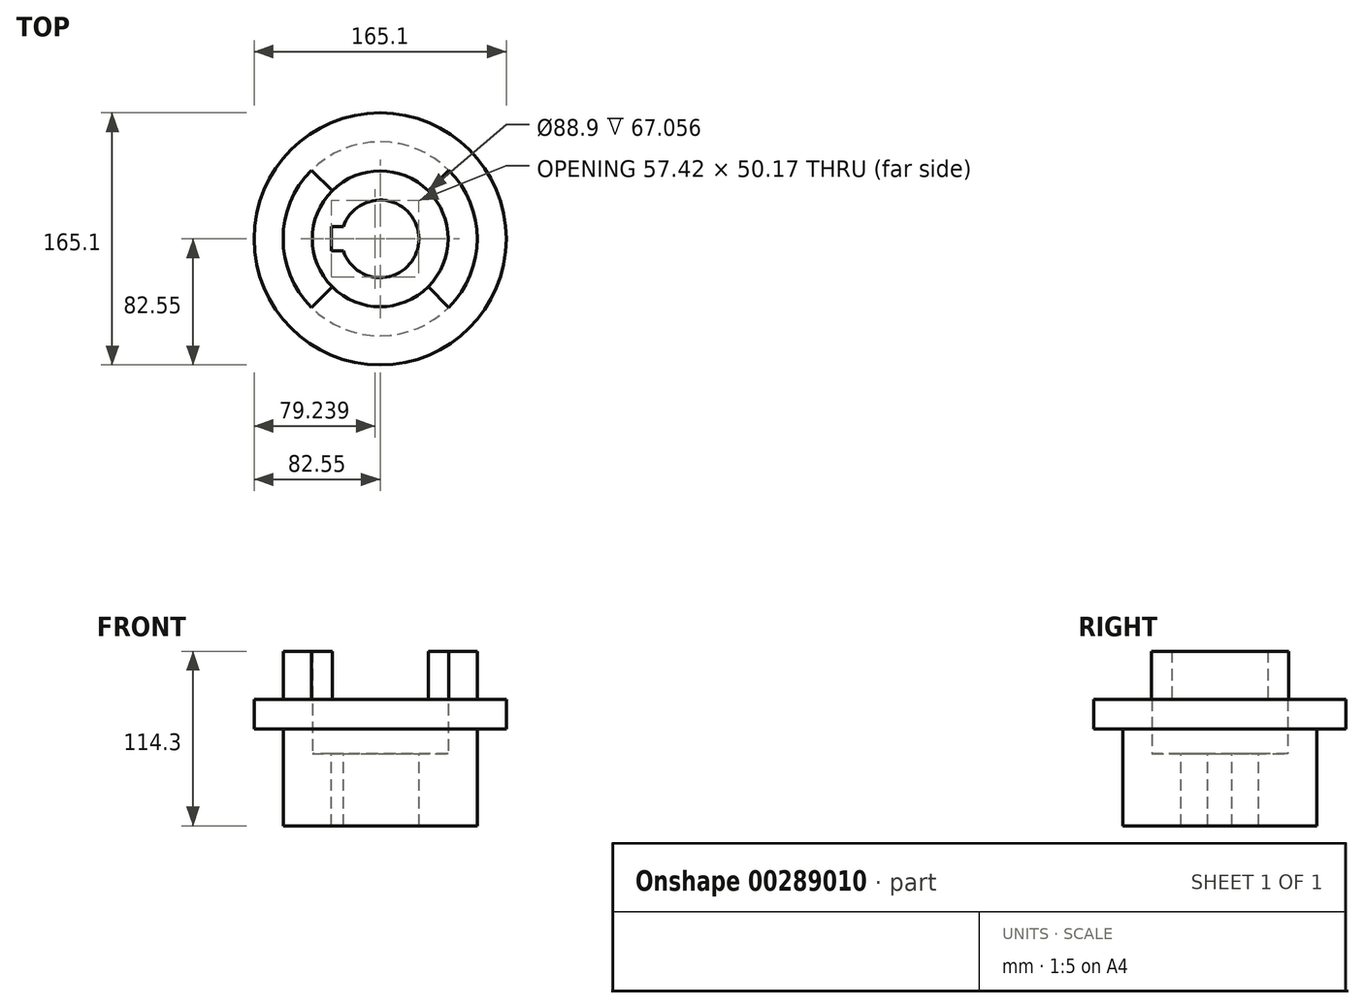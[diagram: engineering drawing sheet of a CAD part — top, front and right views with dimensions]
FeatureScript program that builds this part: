
annotation { "Feature Type Name" : "Feature", "Feature Type Description" : "" }
export const myFeature = defineFeature(function(context is Context, id is Id, definition is map)
    precondition{}
    {
        {
            var Q0;
            Q0=qCreatedBy(makeId("Top.planeOp"),FACE);
            var sketch = newSketch(context, id + "F0", { "sketchPlane" : qUnion([Q0])});
            skCircle(sketch, "E0", {"center": v(0, 0) * mm, "radius": 82.55 * mm});
            skCircle(sketch, "E1", {"center": v(0, 0) * mm, "radius": 63.5 * mm});
            skCircle(sketch, "E2", {"center": v(0, 0) * mm, "radius": 44.45 * mm});
            skCircle(sketch, "E3", {"center": v(0, 0) * mm, "radius": 25.4 * mm});
            skLineSegment(sketch, "E4", {"start": v(-24.15, -7.87) * mm, "end": v(-32.02, -7.87) * mm});
            skLineSegment(sketch, "E5", {"start": v(-32.02, -7.87) * mm, "end": v(-32.02, 7.87) * mm});
            skLineSegment(sketch, "E6", {"start": v(-32.02, 7.87) * mm, "end": v(-24.15, 7.87) * mm});
            skLineSegment(sketch, "E7", {"start": v(0, 0) * mm, "end": v(-44.9, 44.9) * mm});
            skLineSegment(sketch, "E8", {"start": v(0, 0) * mm, "end": v(0, 82.55) * mm, "construction": true});
            skLineSegment(sketch, "E9", {"start": v(0, 0) * mm, "end": v(-82.55, 0) * mm, "construction": true});
            skLineSegment(sketch, "E10.0.MirrorCS", {"start": v(0, 0) * mm, "end": v(-44.9, -44.9) * mm});
            skLineSegment(sketch, "E11.0.MirrorCS", {"start": v(0, 0) * mm, "end": v(44.9, 44.9) * mm});
            skLineSegment(sketch, "E12.0.MirrorCS", {"start": v(0, 0) * mm, "end": v(44.9, -44.9) * mm});
            skSolve(sketch);
        }
        {
            var Q0;
            {var subQ5=sQuery(id+"F0.wireOp",EDGE,"E4");Q0=makeQuery(id+"F0.imprint","IMPRINT",FACE,{"disambiguationData":[TD([[makeQuery(id+"F0.imprint","IMPRINT",EDGE,{"derivedFrom":subQ5}),1.0]])]});}
            var Q1;
            {var subQ3=sQuery(id+"F0.wireOp",EDGE,"E1");var subQ5=sQuery(id+"F0.wireOp",EDGE,"E7");var subQ7=makeQuery(id+"F0.imprint","INTERSECT",VERTEX,{"derivedFrom":[subQ3,subQ5]});Q1=makeQuery(id+"F0.imprint","IMPRINT",FACE,{"disambiguationData":[TD([[makeQuery(id+"F0.imprint","IMPRINT",EDGE,{"disambiguationData":[TD([[subQ7,-1.0]])],"derivedFrom":subQ3}),1.0]])]});}
            var Q2;
            {var subQ3=sQuery(id+"F0.wireOp",EDGE,"E1");var subQ5=sQuery(id+"F0.wireOp",EDGE,"E7");var subQ7=makeQuery(id+"F0.imprint","INTERSECT",VERTEX,{"derivedFrom":[subQ3,subQ5]});Q2=makeQuery(id+"F0.imprint","IMPRINT",FACE,{"disambiguationData":[TD([[makeQuery(id+"F0.imprint","IMPRINT",EDGE,{"disambiguationData":[TD([[subQ7,1.0]])],"derivedFrom":subQ3}),1.0]])]});}
            var Q3;
            {var subQ3=sQuery(id+"F0.wireOp",EDGE,"E2");var subQ5=sQuery(id+"F0.wireOp",EDGE,"E7");var subQ7=makeQuery(id+"F0.imprint","INTERSECT",VERTEX,{"derivedFrom":[subQ3,subQ5]});Q3=makeQuery(id+"F0.imprint","IMPRINT",FACE,{"disambiguationData":[TD([[makeQuery(id+"F0.imprint","IMPRINT",EDGE,{"disambiguationData":[TD([[subQ7,1.0]])],"derivedFrom":subQ3}),1.0]])]});}
            var Q4;
            {var subQ3=sQuery(id+"F0.wireOp",EDGE,"E2");var subQ5=sQuery(id+"F0.wireOp",EDGE,"E10.0.MirrorCS");var subQ7=makeQuery(id+"F0.imprint","INTERSECT",VERTEX,{"derivedFrom":[subQ3,subQ5]});Q4=makeQuery(id+"F0.imprint","IMPRINT",FACE,{"disambiguationData":[TD([[makeQuery(id+"F0.imprint","IMPRINT",EDGE,{"disambiguationData":[TD([[subQ7,-1.0]])],"derivedFrom":subQ3}),1.0]])]});}
            var Q5;
            {var subQ3=sQuery(id+"F0.wireOp",EDGE,"E1");var subQ5=sQuery(id+"F0.wireOp",EDGE,"E10.0.MirrorCS");var subQ7=makeQuery(id+"F0.imprint","INTERSECT",VERTEX,{"derivedFrom":[subQ3,subQ5]});Q5=makeQuery(id+"F0.imprint","IMPRINT",FACE,{"disambiguationData":[TD([[makeQuery(id+"F0.imprint","IMPRINT",EDGE,{"disambiguationData":[TD([[subQ7,-1.0]])],"derivedFrom":subQ3}),1.0]])]});}
            var Q6;
            {var subQ3=sQuery(id+"F0.wireOp",EDGE,"E2");var subQ5=sQuery(id+"F0.wireOp",EDGE,"E11.0.MirrorCS");var subQ7=makeQuery(id+"F0.imprint","INTERSECT",VERTEX,{"derivedFrom":[subQ3,subQ5]});Q6=makeQuery(id+"F0.imprint","IMPRINT",FACE,{"disambiguationData":[TD([[makeQuery(id+"F0.imprint","IMPRINT",EDGE,{"disambiguationData":[TD([[subQ7,1.0]])],"derivedFrom":subQ3}),1.0]])]});}
            var Q7;
            {var subQ3=sQuery(id+"F0.wireOp",EDGE,"E1");var subQ5=sQuery(id+"F0.wireOp",EDGE,"E11.0.MirrorCS");var subQ7=makeQuery(id+"F0.imprint","INTERSECT",VERTEX,{"derivedFrom":[subQ3,subQ5]});Q7=makeQuery(id+"F0.imprint","IMPRINT",FACE,{"disambiguationData":[TD([[makeQuery(id+"F0.imprint","IMPRINT",EDGE,{"disambiguationData":[TD([[subQ7,1.0]])],"derivedFrom":subQ3}),1.0]])]});}
            extrude(context, id + "F1", {"entities" : qUnion([Q0, Q1, Q2, Q3, Q4, Q5, Q6, Q7]), "oppositeDirection" : true, "depth" : 63.5 * mm});
        }
        {
            var Q0;
            Q0=makeQuery(id+"F0.imprint","IMPRINT",FACE,{"disambiguationData":[TD([[makeQuery(id+"F0.imprint","IMPRINT",EDGE,{"derivedFrom":sQuery(id+"F0.wireOp",EDGE,"E0")}),1.0]])]});
            var Q1;
            {var subQ3=sQuery(id+"F0.wireOp",EDGE,"E1");var subQ5=sQuery(id+"F0.wireOp",EDGE,"E7");var subQ7=makeQuery(id+"F0.imprint","INTERSECT",VERTEX,{"derivedFrom":[subQ3,subQ5]});Q1=makeQuery(id+"F0.imprint","IMPRINT",FACE,{"disambiguationData":[TD([[makeQuery(id+"F0.imprint","IMPRINT",EDGE,{"disambiguationData":[TD([[subQ7,-1.0]])],"derivedFrom":subQ3}),1.0]])]});}
            var Q2;
            {var subQ3=sQuery(id+"F0.wireOp",EDGE,"E1");var subQ5=sQuery(id+"F0.wireOp",EDGE,"E7");var subQ7=makeQuery(id+"F0.imprint","INTERSECT",VERTEX,{"derivedFrom":[subQ3,subQ5]});Q2=makeQuery(id+"F0.imprint","IMPRINT",FACE,{"disambiguationData":[TD([[makeQuery(id+"F0.imprint","IMPRINT",EDGE,{"disambiguationData":[TD([[subQ7,1.0]])],"derivedFrom":subQ3}),1.0]])]});}
            var Q3;
            {var subQ3=sQuery(id+"F0.wireOp",EDGE,"E1");var subQ5=sQuery(id+"F0.wireOp",EDGE,"E10.0.MirrorCS");var subQ7=makeQuery(id+"F0.imprint","INTERSECT",VERTEX,{"derivedFrom":[subQ3,subQ5]});Q3=makeQuery(id+"F0.imprint","IMPRINT",FACE,{"disambiguationData":[TD([[makeQuery(id+"F0.imprint","IMPRINT",EDGE,{"disambiguationData":[TD([[subQ7,-1.0]])],"derivedFrom":subQ3}),1.0]])]});}
            var Q4;
            {var subQ3=sQuery(id+"F0.wireOp",EDGE,"E1");var subQ5=sQuery(id+"F0.wireOp",EDGE,"E11.0.MirrorCS");var subQ7=makeQuery(id+"F0.imprint","INTERSECT",VERTEX,{"derivedFrom":[subQ3,subQ5]});Q4=makeQuery(id+"F0.imprint","IMPRINT",FACE,{"disambiguationData":[TD([[makeQuery(id+"F0.imprint","IMPRINT",EDGE,{"disambiguationData":[TD([[subQ7,1.0]])],"derivedFrom":subQ3}),1.0]])]});}
            extrude(context, id + "F2", {"entities" : qUnion([Q0, Q1, Q2, Q3, Q4]), "operationType" : NewBodyOperationType.ADD, "depth" : 19.3 * mm});
        }
        {
            var Q0;
            {var subQ3=sQuery(id+"F0.wireOp",EDGE,"E1");var subQ5=sQuery(id+"F0.wireOp",EDGE,"E7");var subQ7=makeQuery(id+"F0.imprint","INTERSECT",VERTEX,{"derivedFrom":[subQ3,subQ5]});Q0=makeQuery(id+"F0.imprint","IMPRINT",FACE,{"disambiguationData":[TD([[makeQuery(id+"F0.imprint","IMPRINT",EDGE,{"disambiguationData":[TD([[subQ7,-1.0]])],"derivedFrom":subQ3}),1.0]])]});}
            var Q1;
            {var subQ3=sQuery(id+"F0.wireOp",EDGE,"E1");var subQ5=sQuery(id+"F0.wireOp",EDGE,"E11.0.MirrorCS");var subQ7=makeQuery(id+"F0.imprint","INTERSECT",VERTEX,{"derivedFrom":[subQ3,subQ5]});Q1=makeQuery(id+"F0.imprint","IMPRINT",FACE,{"disambiguationData":[TD([[makeQuery(id+"F0.imprint","IMPRINT",EDGE,{"disambiguationData":[TD([[subQ7,1.0]])],"derivedFrom":subQ3}),1.0]])]});}
            extrude(context, id + "F3", {"entities" : qUnion([Q0, Q1]), "operationType" : NewBodyOperationType.ADD, "depth" : 50.8 * mm});
        }
        {
            var Q0;
            Q0=makeQuery(id+"F1.opExtrude","CAP_FACE",FACE,{"disambiguationData":[OSD([sQuery(id+"F0.wireOp",EDGE,"E1"),sQuery(id+"F0.wireOp",EDGE,"E3"),sQuery(id+"F0.wireOp",EDGE,"E4"),sQuery(id+"F0.wireOp",EDGE,"E5"),sQuery(id+"F0.wireOp",EDGE,"E6")])],"isStart":true});
            extrude(context, id + "F4", {"entities" : qUnion([Q0]), "operationType" : NewBodyOperationType.REMOVE, "oppositeDirection" : true, "depth" : 16.26 * mm});
        }
    });
